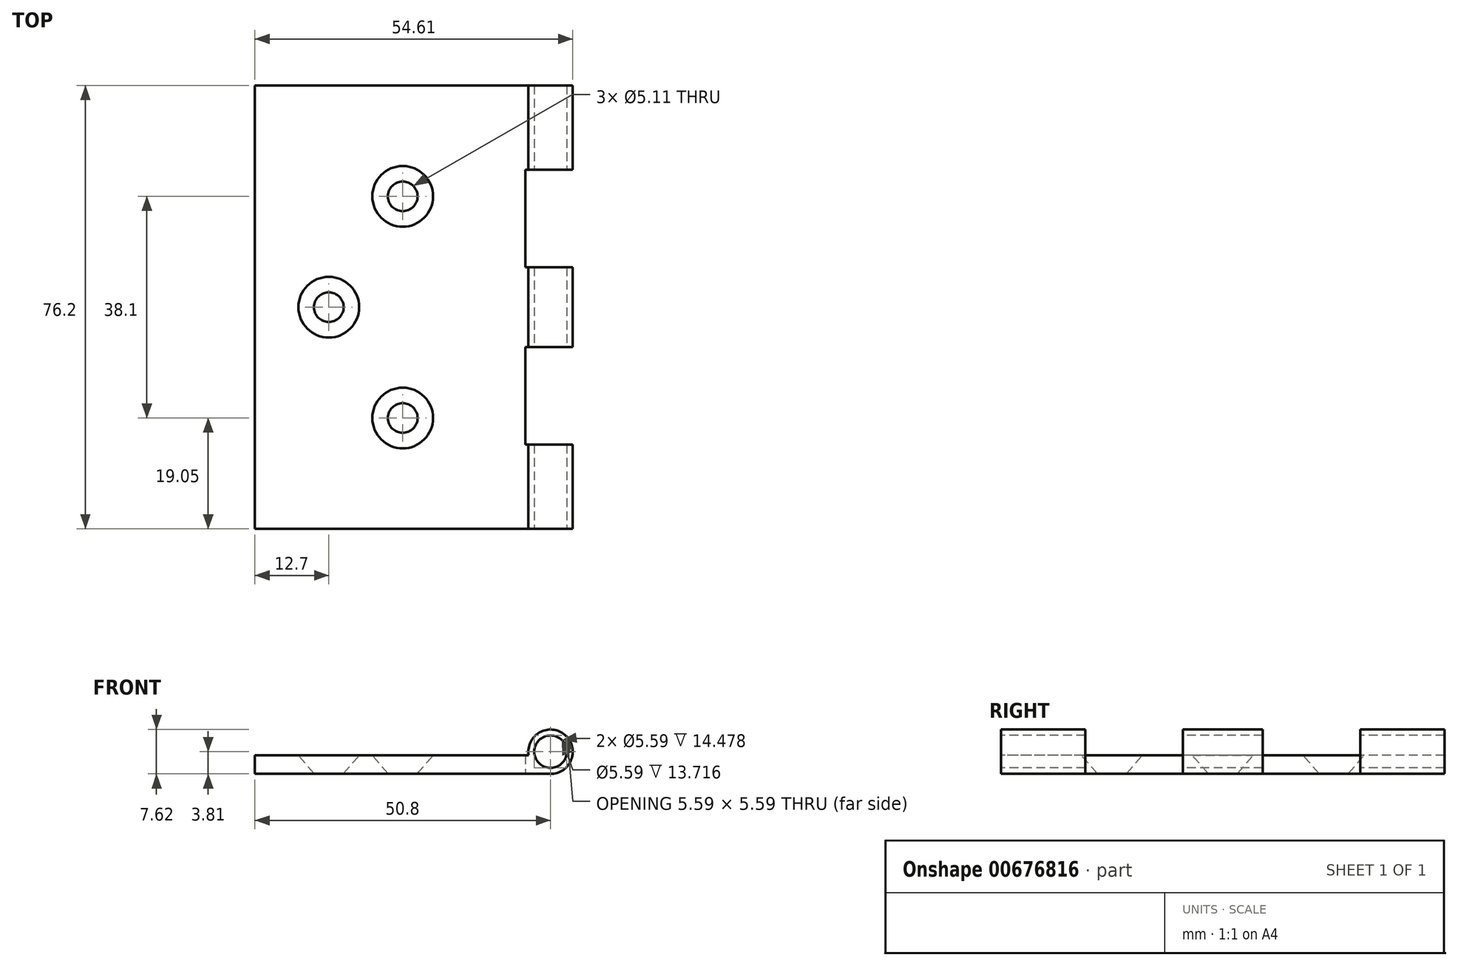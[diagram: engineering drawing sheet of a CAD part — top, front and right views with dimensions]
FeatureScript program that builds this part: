
annotation { "Feature Type Name" : "Feature", "Feature Type Description" : "" }
export const myFeature = defineFeature(function(context is Context, id is Id, definition is map)
    precondition{}
    {
        {
            var Q0;
            Q0=qCreatedBy(makeId("Top.planeOp"),FACE);
            var sketch = newSketch(context, id + "F0", { "sketchPlane" : qUnion([Q0])});
            skLineSegment(sketch, "E0.bottom", {"start": v(0, 0) * mm, "end": v(-50.8, 0) * mm});
            skLineSegment(sketch, "E0.top", {"start": v(0, 76.2) * mm, "end": v(-50.8, 76.2) * mm});
            skLineSegment(sketch, "E0.left", {"start": v(0, 0) * mm, "end": v(0, 76.2) * mm});
            skLineSegment(sketch, "E0.right", {"start": v(-50.8, 0) * mm, "end": v(-50.8, 76.2) * mm});
            skSolve(sketch);
        }
        {
            var Q0;
            Q0=makeQuery(id+"F0.imprint","IMPRINT",FACE,{"disambiguationData":[TD([[makeQuery(id+"F0.imprint","IMPRINT",EDGE,{"derivedFrom":sQuery(id+"F0.wireOp",EDGE,"E0.bottom")}),-1.0]])]});
            extrude(context, id + "F1", {"entities" : qUnion([Q0]), "oppositeDirection" : true, "depth" : 3.17 * mm, "offsetDistance" : 25.4 * mm});
        }
        {
            var Q0;
            Q0=makeQuery(id+"F1.opExtrude","SWEPT_FACE",FACE,{"disambiguationData":[OSD([sQuery(id+"F0.wireOp",EDGE,"E0.top")])]});
            var sketch = newSketch(context, id + "F2", { "sketchPlane" : qUnion([Q0])});
            skLineSegment(sketch, "E1", {"start": v(0, 0) * mm, "end": v(0, -0.63) * mm});
            skCircle(sketch, "E2", {"center": v(0, -3.81) * mm, "radius": 3.81 * mm});
            skLineSegment(sketch, "E3.trimOffspring", {"start": v(0, -6.99) * mm, "end": v(0, -7.62) * mm});
            skCircle(sketch, "E4", {"center": v(0, -3.81) * mm, "radius": 2.8 * mm});
            skSolve(sketch);
        }
        {
            var Q0;
            {var subQ0=sQuery(id+"F2.wireOp",EDGE,"E3.trimOffspring");Q0=makeQuery(id+"F2.imprint","IMPRINT",FACE,{"disambiguationData":[TD([[makeQuery(id+"F2.imprint","IMPRINT",EDGE,{"derivedFrom":subQ0}),1.0]])]});}
            var Q1;
            {var subQ0=sQuery(id+"F2.wireOp",EDGE,"E1");Q1=makeQuery(id+"F2.imprint","IMPRINT",FACE,{"disambiguationData":[TD([[makeQuery(id+"F2.imprint","IMPRINT",EDGE,{"derivedFrom":subQ0}),-1.0]])]});}
            var Q2;
            {var subQ0=sQuery(id+"F2.wireOp",EDGE,"E1");Q2=makeQuery(id+"F2.imprint","IMPRINT",FACE,{"disambiguationData":[TD([[makeQuery(id+"F2.imprint","IMPRINT",EDGE,{"derivedFrom":subQ0}),1.0]])]});}
            extrude(context, id + "F3", {"entities" : qUnion([Q0, Q1, Q2]), "operationType" : NewBodyOperationType.ADD, "oppositeDirection" : true, "depth" : 76.2 * mm, "offsetDistance" : 25.4 * mm});
        }
        {
            var Q0;
            {var subQ0=sQuery(id+"F2.wireOp",EDGE,"bk9SJdQ4-HYpW-rmkn-T37I-xSyrIBaaHA8p");var subQ1=sQuery(id+"F0.wireOp",EDGE,"E0.top");var subQ4=makeQuery(id+"F1.opExtrude","CAP_EDGE",EDGE,{"disambiguationData":[OSD([subQ1])],"isStart":false});var subQ5=makeQuery(id+"F2.imprint","INTERSECT",VERTEX,{"derivedFrom":[subQ4,subQ0]});Q0=makeQuery(id+"F2.imprint","IMPRINT",FACE,{"disambiguationData":[TD([[makeQuery(id+"F2.imprint","IMPRINT",EDGE,{"disambiguationData":[TD([[subQ5,1.0]])],"derivedFrom":subQ4}),1.0]])]});}
            extrude(context, id + "F4", {"entities" : qUnion([Q0]), "operationType" : NewBodyOperationType.REMOVE, "oppositeDirection" : true, "depth" : 76.2 * mm, "offsetDistance" : 25.4 * mm});
        }
        {
            var Q0;
            Q0=makeQuery(id+"F1.opExtrude","SWEPT_BODY",BODY,{"disambiguationData":[OSD([sQuery(id+"F0.wireOp",EDGE,"E0.bottom"),sQuery(id+"F0.wireOp",EDGE,"E0.top"),sQuery(id+"F0.wireOp",EDGE,"E0.left"),sQuery(id+"F0.wireOp",EDGE,"E0.right")])]});
            transform(context, id + "F5", {"entities" : qUnion([Q0]), "transformType" : TransformType.TRANSLATION_3D, "dx" : 63.5 * mm, "dy" : 0 * mm, "dz" : 0 * mm, "makeCopy" : true});
        }
        {
            var Q0;
            Q0=makeQuery(id+"F5.opPattern","COPY",BODY,{"derivedFrom":makeQuery(id+"F1.opExtrude","SWEPT_BODY",BODY,{"disambiguationData":[OSD([sQuery(id+"F0.wireOp",EDGE,"E0.bottom"),sQuery(id+"F0.wireOp",EDGE,"E0.top"),sQuery(id+"F0.wireOp",EDGE,"E0.left"),sQuery(id+"F0.wireOp",EDGE,"E0.right")])]}),"instanceName":"1"});
            transform(context, id + "F6", {"entities" : qUnion([Q0]), "transformType" : TransformType.TRANSLATION_3D, "dx" : 0 * mm, "dy" : 0 * mm, "dz" : 0 * mm, "makeCopy" : true});
        }
        {
            var Q0;
            Q0=makeQuery(id+"F6.opPattern","COPY",BODY,{"derivedFrom":makeQuery(id+"F5.opPattern","COPY",BODY,{"derivedFrom":makeQuery(id+"F1.opExtrude","SWEPT_BODY",BODY,{"disambiguationData":[OSD([sQuery(id+"F0.wireOp",EDGE,"E0.bottom"),sQuery(id+"F0.wireOp",EDGE,"E0.top"),sQuery(id+"F0.wireOp",EDGE,"E0.left"),sQuery(id+"F0.wireOp",EDGE,"E0.right")])]}),"instanceName":"1"}),"instanceName":"1"});
            deleteBodies(context, id + "F7", {"entities" : qUnion([Q0])});
        }
        {
            var Q0;
            Q0=makeQuery(id+"F5.opPattern","COPY",FACE,{"derivedFrom":makeQuery(id+"F3.boolean.opBoolean","MERGE",FACE,{"derivedFrom":[makeQuery(id+"F1.opExtrude","SWEPT_FACE",FACE,{"disambiguationData":[OSD([sQuery(id+"F0.wireOp",EDGE,"E0.top")])]}),makeQuery(id+"F3.opExtrude","CAP_FACE",FACE,{"disambiguationData":[OSD([sQuery(id+"F2.wireOp",EDGE,"E2"),sQuery(id+"F2.wireOp",EDGE,"bk9SJdQ4-HYpW-rmkn-T37I-xSyrIBaaHA8p")])],"isStart":true})]}),"instanceName":"1"});
            var sketch = newSketch(context, id + "F8", { "sketchPlane" : qUnion([Q0])});
            skLineSegment(sketch, "E5", {"start": v(-12.7, 0) * mm, "end": v(-12.7, -22) * mm});
            skSolve(sketch);
        }
        {
            var Q0;
            Q0=makeQuery(id+"F5.opPattern","COPY",BODY,{"derivedFrom":makeQuery(id+"F1.opExtrude","SWEPT_BODY",BODY,{"disambiguationData":[OSD([sQuery(id+"F0.wireOp",EDGE,"E0.bottom"),sQuery(id+"F0.wireOp",EDGE,"E0.top"),sQuery(id+"F0.wireOp",EDGE,"E0.left"),sQuery(id+"F0.wireOp",EDGE,"E0.right")])]}),"instanceName":"1"});
            var Q1;
            Q1=sQuery(id+"F8.wireOp",EDGE,"E5");
            transform(context, id + "F9", {"entities" : qUnion([Q0]), "transformType" : TransformType.ROTATION, "transformAxis" : qUnion([Q1]), "angle" : 180 * degree, "makeCopy" : false});
        }
        {
            var Q0;
            Q0=makeQuery(id+"F5.opPattern","COPY",BODY,{"derivedFrom":makeQuery(id+"F1.opExtrude","SWEPT_BODY",BODY,{"disambiguationData":[OSD([sQuery(id+"F0.wireOp",EDGE,"E0.bottom"),sQuery(id+"F0.wireOp",EDGE,"E0.top"),sQuery(id+"F0.wireOp",EDGE,"E0.left"),sQuery(id+"F0.wireOp",EDGE,"E0.right")])]}),"instanceName":"1"});
            transform(context, id + "F10", {"entities" : qUnion([Q0]), "transformType" : TransformType.TRANSLATION_3D, "dx" : 50.8 * mm, "dy" : -76.2 * mm, "dz" : 0 * mm, "makeCopy" : false});
        }
        {
            var Q0;
            Q0=makeQuery(id+"F3.boolean.opBoolean","MERGE",FACE,{"derivedFrom":[makeQuery(id+"F1.opExtrude","SWEPT_FACE",FACE,{"disambiguationData":[OSD([sQuery(id+"F0.wireOp",EDGE,"E0.bottom")])]}),makeQuery(id+"F3.opExtrude","CAP_FACE",FACE,{"disambiguationData":[OSD([sQuery(id+"F2.wireOp",EDGE,"E2"),sQuery(id+"F2.wireOp",EDGE,"bk9SJdQ4-HYpW-rmkn-T37I-xSyrIBaaHA8p")])],"isStart":false})]});
            var sketch = newSketch(context, id + "F11", { "sketchPlane" : qUnion([Q0])});
            skPoint(sketch, "E6.start.orphan", {"position": v(0, -3.81) * mm});
            skLineSegment(sketch, "E7", {"start": v(0, -3.81) * mm, "end": v(-3.8, -3.81) * mm});
            skLineSegment(sketch, "E8", {"start": v(-3.8, -3.81) * mm, "end": v(-3.8, 0) * mm});
            skLineSegment(sketch, "E9", {"start": v(-3.8, 0) * mm, "end": v(4.25, 0) * mm});
            skLineSegment(sketch, "E10", {"start": v(0, -3.81) * mm, "end": v(3.81, -3.81) * mm});
            skLineSegment(sketch, "E11", {"start": v(3.81, -3.81) * mm, "end": v(3.81, 0) * mm});
            skSolve(sketch);
        }
        {
            var Q0;
            Q0=sQuery(id+"F0.wireOp",VERTEX,"E0.left.end");
            var Q1;
            Q1=sQuery(id+"F11.wireOp",VERTEX,"E9.end");
            var Q2;
            Q2=sQuery(id+"F11.wireOp",VERTEX,"E8.end");
            cPlane(context, id + "F12", {"entities" : qUnion([Q0, Q1, Q2]), "cplaneType" : CPlaneType.THREE_POINT, "offset" : 25.4 * mm, "width" : 152.4 * mm, "height" : 152.4 * mm});
        }
        {
            var Q0;
            Q0=qCreatedBy(id+"F12.planeOp",FACE);
            var sketch = newSketch(context, id + "F13", { "sketchPlane" : qUnion([Q0])});
            skLineSegment(sketch, "E12", {"start": v(0, 0) * mm, "end": v(3.81, 0) * mm});
            skLineSegment(sketch, "E13", {"start": v(3.81, 0) * mm, "end": v(3.81, 76.2) * mm});
            skLineSegment(sketch, "E14", {"start": v(3.81, 76.2) * mm, "end": v(-3.81, 76.2) * mm});
            skLineSegment(sketch, "E15", {"start": v(-3.81, 76.2) * mm, "end": v(-3.81, 0) * mm});
            skLineSegment(sketch, "E16", {"start": v(-3.81, 0) * mm, "end": v(-3.81, 15.24) * mm});
            skLineSegment(sketch, "E17", {"start": v(-3.81, 15.24) * mm, "end": v(3.81, 15.24) * mm});
            skLineSegment(sketch, "E18", {"start": v(3.81, 15.24) * mm, "end": v(3.81, 30.48) * mm});
            skLineSegment(sketch, "E19", {"start": v(3.81, 30.48) * mm, "end": v(-3.81, 30.48) * mm});
            skLineSegment(sketch, "E20", {"start": v(-3.81, 30.48) * mm, "end": v(-3.81, 45.72) * mm});
            skLineSegment(sketch, "E21", {"start": v(-3.81, 45.72) * mm, "end": v(3.81, 45.72) * mm});
            skLineSegment(sketch, "E22", {"start": v(3.81, 45.72) * mm, "end": v(3.81, 60.96) * mm});
            skLineSegment(sketch, "E23", {"start": v(3.81, 60.96) * mm, "end": v(-3.81, 60.96) * mm});
            skLineSegment(sketch, "E24", {"start": v(3.81, 0) * mm, "end": v(3.81, 15.24) * mm});
            skLineSegment(sketch, "E25", {"start": v(-3.81, 15.24) * mm, "end": v(-3.81, 0) * mm});
            skLineSegment(sketch, "E26", {"start": v(3.81, 0) * mm, "end": v(-3.81, 0) * mm});
            skSolve(sketch);
        }
        {
            var Q0;
            {var subQ0=sQuery(id+"F13.wireOp",EDGE,"E17");Q0=makeQuery(id+"F13.imprint","IMPRINT",FACE,{"disambiguationData":[TD([[makeQuery(id+"F13.imprint","IMPRINT",EDGE,{"derivedFrom":subQ0}),1.0]])]});}
            var Q1;
            {var subQ0=sQuery(id+"F13.wireOp",EDGE,"E21");Q1=makeQuery(id+"F13.imprint","IMPRINT",FACE,{"disambiguationData":[TD([[makeQuery(id+"F13.imprint","IMPRINT",EDGE,{"derivedFrom":subQ0}),1.0]])]});}
            extrude(context, id + "F14", {"entities" : qUnion([Q0, Q1]), "operationType" : NewBodyOperationType.REMOVE, "endBound" : BoundingType.THROUGH_ALL, "oppositeDirection" : true, "depth" : 25.4 * mm, "offsetDistance" : 25.4 * mm});
        }
        {
            var Q0;
            Q0=makeQuery(id+"F5.opPattern","COPY",BODY,{"derivedFrom":makeQuery(id+"F1.opExtrude","SWEPT_BODY",BODY,{"disambiguationData":[OSD([sQuery(id+"F0.wireOp",EDGE,"E0.bottom"),sQuery(id+"F0.wireOp",EDGE,"E0.top"),sQuery(id+"F0.wireOp",EDGE,"E0.left"),sQuery(id+"F0.wireOp",EDGE,"E0.right")])]}),"instanceName":"1"});
            deleteBodies(context, id + "F15", {"entities" : qUnion([Q0])});
        }
        {
            var Q0;
            Q0=makeQuery(id+"F1.opExtrude","SWEPT_BODY",BODY,{"disambiguationData":[OSD([sQuery(id+"F0.wireOp",EDGE,"E0.bottom"),sQuery(id+"F0.wireOp",EDGE,"E0.top"),sQuery(id+"F0.wireOp",EDGE,"E0.left"),sQuery(id+"F0.wireOp",EDGE,"E0.right")])]});
            transform(context, id + "F16", {"entities" : qUnion([Q0]), "transformType" : TransformType.TRANSLATION_3D, "dx" : 63.5 * mm, "dy" : 0 * mm, "dz" : 0 * mm, "makeCopy" : true});
        }
        {
            var Q0;
            Q0=makeQuery(id+"F16.opPattern","COPY",BODY,{"derivedFrom":makeQuery(id+"F1.opExtrude","SWEPT_BODY",BODY,{"disambiguationData":[OSD([sQuery(id+"F0.wireOp",EDGE,"E0.bottom"),sQuery(id+"F0.wireOp",EDGE,"E0.top"),sQuery(id+"F0.wireOp",EDGE,"E0.left"),sQuery(id+"F0.wireOp",EDGE,"E0.right")])]}),"instanceName":"1"});
            deleteBodies(context, id + "F17", {"entities" : qUnion([Q0])});
        }
        {
            var Q0;
            Q0=makeQuery(id+"F1.opExtrude","SWEPT_BODY",BODY,{"disambiguationData":[OSD([sQuery(id+"F0.wireOp",EDGE,"E0.bottom"),sQuery(id+"F0.wireOp",EDGE,"E0.top"),sQuery(id+"F0.wireOp",EDGE,"E0.left"),sQuery(id+"F0.wireOp",EDGE,"E0.right")])]});
            var Q1;
            Q1=sQuery(id+"F0.wireOp",EDGE,"E0.top");
            transform(context, id + "F18", {"entities" : qUnion([Q0]), "transformType" : TransformType.ROTATION, "transformAxis" : qUnion([Q1]), "angle" : 180 * degree, "makeCopy" : false});
        }
        {
            var Q0;
            {var subQ1=sQuery(id+"F0.wireOp",EDGE,"E0.top");var subQ3=sQuery(id+"F0.wireOp",EDGE,"E0.right");var subQ4=sQuery(id+"F0.wireOp",EDGE,"E0.bottom");Q0=makeQuery(id+"F3.boolean.opBoolean","SPLIT",FACE,{"disambiguationData":[TD([makeQuery(id+"F1.opExtrude","SWEPT_FACE",FACE,{"disambiguationData":[OSD([subQ3])]})])],"derivedFrom":makeQuery(id+"F1.opExtrude","CAP_FACE",FACE,{"disambiguationData":[OSD([subQ4,subQ1,sQuery(id+"F0.wireOp",EDGE,"E0.left"),subQ3])],"isStart":false})});}
            var sketch = newSketch(context, id + "F19", { "sketchPlane" : qUnion([Q0])});
            skLineSegment(sketch, "E27", {"start": v(-50.8, 152.4) * mm, "end": v(-25.4, 152.4) * mm});
            skLineSegment(sketch, "E28", {"start": v(-25.4, 152.4) * mm, "end": v(-25.4, 114.3) * mm});
            skLineSegment(sketch, "E29", {"start": v(-25.4, 114.3) * mm, "end": v(-50.8, 114.3) * mm, "construction": true});
            skLineSegment(sketch, "E30", {"start": v(-50.8, 114.3) * mm, "end": v(-38.1, 114.3) * mm, "construction": true});
            skLineSegment(sketch, "E31", {"start": v(-38.1, 114.3) * mm, "end": v(-38.1, 95.25) * mm, "construction": true});
            skLineSegment(sketch, "E32", {"start": v(-38.1, 95.25) * mm, "end": v(-25.4, 95.25) * mm, "construction": true});
            skLineSegment(sketch, "E33", {"start": v(-25.4, 95.25) * mm, "end": v(-25.4, 133.35) * mm, "construction": true});
            skSolve(sketch);
        }
        {
            var Q0;
            Q0=sQuery(id+"F19.wireOp",VERTEX,"E31.start");
            var Q1;
            Q1=sQuery(id+"F19.wireOp",VERTEX,"E33.start");
            var Q2;
            Q2=sQuery(id+"F19.wireOp",VERTEX,"E33.end");
            var Q3;
            Q3=makeQuery(id+"F1.opExtrude","SWEPT_BODY",BODY,{"disambiguationData":[OSD([sQuery(id+"F0.wireOp",EDGE,"E0.bottom"),sQuery(id+"F0.wireOp",EDGE,"E0.top"),sQuery(id+"F0.wireOp",EDGE,"E0.left"),sQuery(id+"F0.wireOp",EDGE,"E0.right")])]});
            hole(context, id + "F20", {"style" : HoleStyle.C_SINK, "endStyle" : HoleEndStyle.THROUGH, "standardTappedOrClearance" : lookupTablePath({ "standard" : "ANSI", "fit" : "Normal (ASME)", "size" : "#10", "type" : "Clearance" }), "standardBlindInLast" : lookupTablePath({ "fit" : "Free", "standard" : "ANSI", "size" : "#10", "type" : "Clearance" }), "holeDiameter" : 5.1 * mm, "cSinkDiameter" : 10.44 * mm, "cSinkAngle" : 82 * degree, "majorDiameter" : 6.35 * mm, "isTappedThrough" : true, "tappedDepth" : 12.7 * mm, "tapClearance" : 3, "locations" : qUnion([Q0, Q1, Q2]), "scope" : qUnion([Q3])});
        }
        {
            var Q0;
            Q0=makeQuery(id+"F14.boolean.opBoolean","COPY",FACE,{"derivedFrom":makeQuery(id+"F14.opExtrude","SWEPT_FACE",FACE,{"disambiguationData":[OSD([sQuery(id+"F13.wireOp",EDGE,"E17")])]})});
            extrude(context, id + "F21", {"entities" : qUnion([Q0]), "operationType" : NewBodyOperationType.REMOVE, "oppositeDirection" : true, "depth" : 0.25 * mm, "offsetDistance" : 25.4 * mm});
        }
        {
            var Q0;
            Q0=makeQuery(id+"F14.boolean.opBoolean","COPY",FACE,{"derivedFrom":makeQuery(id+"F14.opExtrude","SWEPT_FACE",FACE,{"disambiguationData":[OSD([sQuery(id+"F13.wireOp",EDGE,"E21")])]})});
            extrude(context, id + "F22", {"entities" : qUnion([Q0]), "operationType" : NewBodyOperationType.REMOVE, "oppositeDirection" : true, "depth" : 0.25 * mm, "offsetDistance" : 25.4 * mm});
        }
        {
            var Q0;
            Q0=makeQuery(id+"F14.boolean.opBoolean","COPY",FACE,{"derivedFrom":makeQuery(id+"F14.opExtrude","SWEPT_FACE",FACE,{"disambiguationData":[OSD([sQuery(id+"F13.wireOp",EDGE,"E23")])]})});
            extrude(context, id + "F23", {"entities" : qUnion([Q0]), "operationType" : NewBodyOperationType.REMOVE, "oppositeDirection" : true, "depth" : 0.25 * mm, "offsetDistance" : 25.4 * mm});
        }
        {
            var Q0;
            Q0=makeQuery(id+"F14.boolean.opBoolean","COPY",FACE,{"derivedFrom":makeQuery(id+"F14.opExtrude","SWEPT_FACE",FACE,{"disambiguationData":[OSD([sQuery(id+"F13.wireOp",EDGE,"E19")])]})});
            extrude(context, id + "F24", {"entities" : qUnion([Q0]), "operationType" : NewBodyOperationType.REMOVE, "oppositeDirection" : true, "depth" : 0.25 * mm, "offsetDistance" : 25.4 * mm});
        }
        {
            var Q0;
            Q0=makeQuery(id+"F1.opExtrude","CAP_FACE",FACE,{"disambiguationData":[OSD([sQuery(id+"F0.wireOp",EDGE,"E0.bottom"),sQuery(id+"F0.wireOp",EDGE,"E0.top"),sQuery(id+"F0.wireOp",EDGE,"E0.left"),sQuery(id+"F0.wireOp",EDGE,"E0.right")])],"isStart":true});
            var sketch = newSketch(context, id + "F25", { "sketchPlane" : qUnion([Q0])});
            skLineSegment(sketch, "E34", {"start": v(0, -152.4) * mm, "end": v(-3.81, -137.41) * mm});
            skLineSegment(sketch, "E35.bottom", {"start": v(-3.81, -137.41) * mm, "end": v(-4.32, -137.41) * mm});
            skLineSegment(sketch, "E35.top", {"start": v(-3.81, -121.67) * mm, "end": v(-4.32, -121.67) * mm});
            skLineSegment(sketch, "E35.left", {"start": v(-3.81, -137.41) * mm, "end": v(-3.81, -121.67) * mm});
            skLineSegment(sketch, "E35.right", {"start": v(-4.32, -137.41) * mm, "end": v(-4.32, -121.67) * mm});
            skLineSegment(sketch, "E36.bottom", {"start": v(-3.81, -106.93) * mm, "end": v(-4.32, -106.93) * mm});
            skLineSegment(sketch, "E36.top", {"start": v(-3.81, -91.19) * mm, "end": v(-4.32, -91.19) * mm});
            skLineSegment(sketch, "E36.left", {"start": v(-3.81, -106.93) * mm, "end": v(-3.81, -91.19) * mm});
            skLineSegment(sketch, "E36.right", {"start": v(-4.32, -106.93) * mm, "end": v(-4.32, -91.19) * mm});
            skSolve(sketch);
        }
        {
            var Q0;
            Q0 = qSketchRegion(id + "F25", true);
            extrude(context, id + "F26", {"entities" : qUnion([Q0]), "operationType" : NewBodyOperationType.REMOVE, "endBound" : BoundingType.THROUGH_ALL, "oppositeDirection" : true, "depth" : 25.4 * mm, "offsetDistance" : 25.4 * mm});
        }
        {
            var Q0;
            Q0=makeQuery(id+"F26.boolean.opBoolean","MERGE",FACE,{"derivedFrom":[makeQuery(id+"F21.boolean.opBoolean","COPY",FACE,{"derivedFrom":makeQuery(id+"F21.opExtrude","CAP_FACE",FACE,{"disambiguationData":[OSD([sQuery(id+"F13.wireOp",EDGE,"E17")])],"isStart":false})}),makeQuery(id+"F26.opExtrude","SWEPT_FACE",FACE,{"disambiguationData":[OSD([sQuery(id+"F25.wireOp",EDGE,"E35.bottom")])]})]});
            var Q1;
            Q1=makeQuery(id+"F26.boolean.opBoolean","MERGE",FACE,{"derivedFrom":[makeQuery(id+"F22.boolean.opBoolean","COPY",FACE,{"derivedFrom":makeQuery(id+"F22.opExtrude","CAP_FACE",FACE,{"disambiguationData":[OSD([sQuery(id+"F13.wireOp",EDGE,"E21")])],"isStart":false})}),makeQuery(id+"F26.opExtrude","SWEPT_FACE",FACE,{"disambiguationData":[OSD([sQuery(id+"F25.wireOp",EDGE,"E36.bottom")])]})]});
            var Q2;
            Q2=makeQuery(id+"F26.boolean.opBoolean","MERGE",FACE,{"derivedFrom":[makeQuery(id+"F23.boolean.opBoolean","COPY",FACE,{"derivedFrom":makeQuery(id+"F23.opExtrude","CAP_FACE",FACE,{"disambiguationData":[OSD([sQuery(id+"F13.wireOp",EDGE,"E23")])],"isStart":false})}),makeQuery(id+"F26.opExtrude","SWEPT_FACE",FACE,{"disambiguationData":[OSD([sQuery(id+"F25.wireOp",EDGE,"E36.top")])]})]});
            var Q3;
            Q3=makeQuery(id+"F26.boolean.opBoolean","MERGE",FACE,{"derivedFrom":[makeQuery(id+"F24.boolean.opBoolean","COPY",FACE,{"derivedFrom":makeQuery(id+"F24.opExtrude","CAP_FACE",FACE,{"disambiguationData":[OSD([sQuery(id+"F13.wireOp",EDGE,"E19")])],"isStart":false})}),makeQuery(id+"F26.opExtrude","SWEPT_FACE",FACE,{"disambiguationData":[OSD([sQuery(id+"F25.wireOp",EDGE,"E35.top")])]})]});
            extrude(context, id + "F27", {"entities" : qUnion([Q0, Q1, Q2, Q3]), "operationType" : NewBodyOperationType.REMOVE, "oppositeDirection" : true, "depth" : 0.5 * mm, "offsetDistance" : 25.4 * mm});
        }
        {
            var Q0;
            Q0=makeQuery(id+"F26.boolean.opBoolean","MERGE",FACE,{"derivedFrom":[makeQuery(id+"F24.boolean.opBoolean","COPY",FACE,{"derivedFrom":makeQuery(id+"F24.opExtrude","CAP_FACE",FACE,{"disambiguationData":[OSD([sQuery(id+"F13.wireOp",EDGE,"E19")])],"isStart":false})}),makeQuery(id+"F26.opExtrude","SWEPT_FACE",FACE,{"disambiguationData":[OSD([sQuery(id+"F25.wireOp",EDGE,"E35.top")])]})]});
            var Q1;
            Q1=makeQuery(id+"F26.boolean.opBoolean","MERGE",FACE,{"derivedFrom":[makeQuery(id+"F23.boolean.opBoolean","COPY",FACE,{"derivedFrom":makeQuery(id+"F23.opExtrude","CAP_FACE",FACE,{"disambiguationData":[OSD([sQuery(id+"F13.wireOp",EDGE,"E23")])],"isStart":false})}),makeQuery(id+"F26.opExtrude","SWEPT_FACE",FACE,{"disambiguationData":[OSD([sQuery(id+"F25.wireOp",EDGE,"E36.top")])]})]});
            extrude(context, id + "F28", {"entities" : qUnion([Q0, Q1]), "operationType" : NewBodyOperationType.REMOVE, "oppositeDirection" : true, "depth" : 0.5 * mm, "offsetDistance" : 25.4 * mm});
        }
    });
